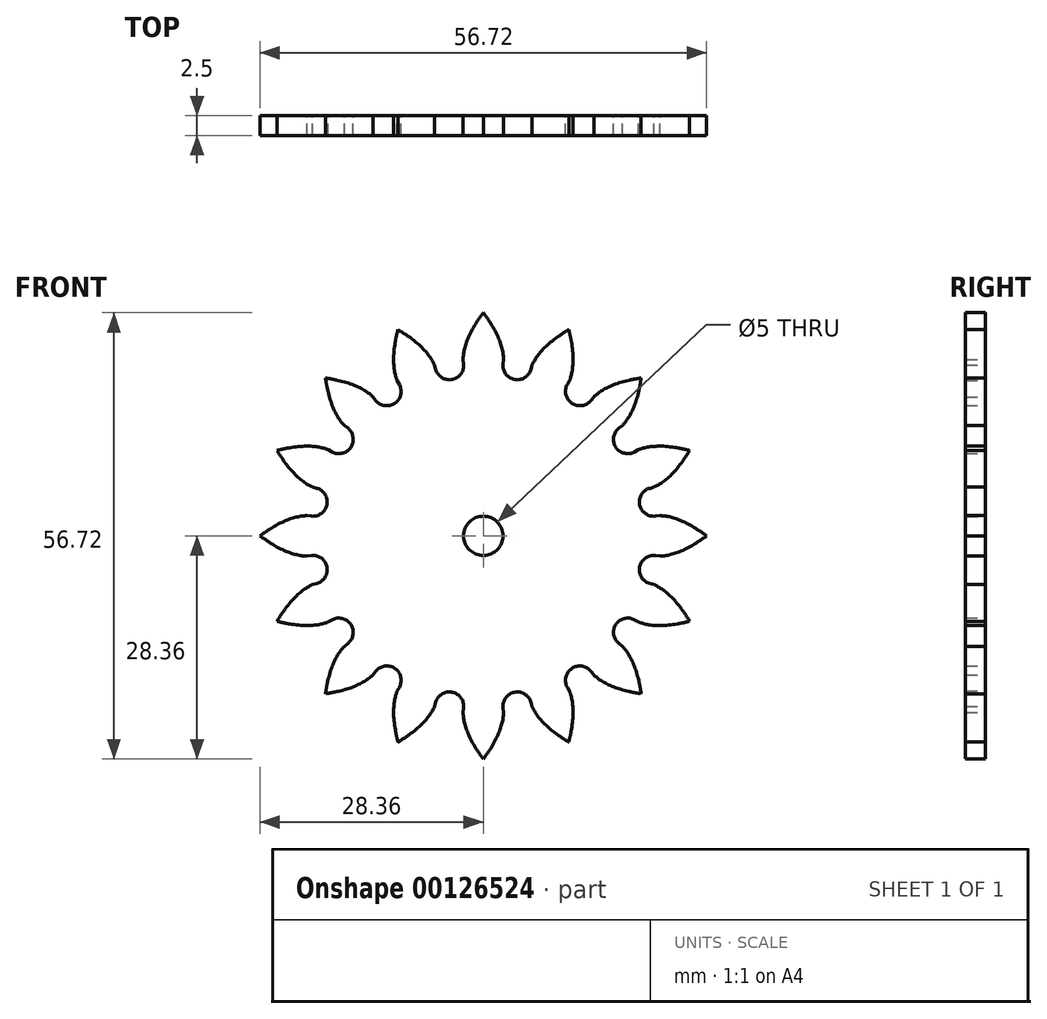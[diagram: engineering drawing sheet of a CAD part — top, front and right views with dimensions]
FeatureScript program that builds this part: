
annotation { "Feature Type Name" : "Feature", "Feature Type Description" : "" }
export const myFeature = defineFeature(function(context is Context, id is Id, definition is map)
    precondition{}
    {
        {
            assignVariable(context, id + "F0", {"name" : "NumberOfTeeth", "anyValue" : 16});
        }
        {
            var Q0;
            Q0=qCreatedBy(makeId("Front.planeOp"),FACE);
            var sketch = newSketch(context, id + "F1", { "sketchPlane" : qUnion([Q0])});
            skCircle(sketch, "E0", {"center": v(0, 0) * mm, "radius": 20.25 * mm});
            skSolve(sketch);
        }
        {
            var Q0;
            Q0=qSketchRegion(id+"F1",true);
            extrude(context, id + "F2", {"entities" : qUnion([Q0]), "depth" : 2.5 * mm});
        }
        {
            var Q0;
            Q0=qCreatedBy(makeId("Front.planeOp"),FACE);
            var sketch = newSketch(context, id + "F3", { "sketchPlane" : qUnion([Q0])});
            skCircle(sketch, "E1", {"center": v(0, 0) * mm, "radius": 24 * mm, "construction": true});
            skLineSegment(sketch, "E2", {"start": v(0, 0) * mm, "end": v(2.35, 23.88) * mm, "construction": true});
            skCircle(sketch, "E3.0", {"center": v(0, 0) * mm, "radius": 20.25 * mm, "construction": true});
            skLineSegment(sketch, "E4", {"start": v(0, 0) * mm, "end": v(4.68, 23.54) * mm, "construction": true});
            skCircle(sketch, "E5", {"center": v(0, 0) * mm, "radius": 22.55 * mm, "construction": true});
            skLineSegment(sketch, "E6", {"start": v(0, 0) * mm, "end": v(2.57, 22.4) * mm, "construction": true});
            skLineSegment(sketch, "E7", {"start": v(0, 0) * mm, "end": v(-3.43, 22.29) * mm, "construction": true});
            skLineSegment(sketch, "E8", {"start": v(0, 0) * mm, "end": v(-9.19, 20.6) * mm, "construction": true});
            skLineSegment(sketch, "E9", {"start": v(0, 0) * mm, "end": v(-14.3, 17.44) * mm, "construction": true});
            skLineSegment(sketch, "E10", {"start": v(0, 0) * mm, "end": v(-18.39, 13.06) * mm, "construction": true});
            skLineSegment(sketch, "E11", {"start": v(2.57, 22.4) * mm, "end": v(-3.43, 22.29) * mm, "construction": true});
            skLineSegment(sketch, "E12", {"start": v(-3.43, 22.29) * mm, "end": v(-9.19, 20.6) * mm, "construction": true});
            skLineSegment(sketch, "E13", {"start": v(-9.19, 20.6) * mm, "end": v(-14.3, 17.44) * mm, "construction": true});
            skLineSegment(sketch, "E14", {"start": v(-14.3, 17.44) * mm, "end": v(-18.39, 13.06) * mm, "construction": true});
            skLineSegment(sketch, "E15", {"start": v(0, 0) * mm, "end": v(-21.18, 7.75) * mm, "construction": true});
            skLineSegment(sketch, "E16", {"start": v(-18.39, 13.06) * mm, "end": v(-21.18, 7.75) * mm, "construction": true});
            skLineSegment(sketch, "E17", {"start": v(-3.43, 22.29) * mm, "end": v(2.5, 23.2) * mm, "construction": true});
            skLineSegment(sketch, "E18", {"start": v(-9.19, 20.6) * mm, "end": v(1.77, 25.49) * mm, "construction": true});
            skLineSegment(sketch, "E19", {"start": v(-14.3, 17.44) * mm, "end": v(-0.37, 28.85) * mm, "construction": true});
            skLineSegment(sketch, "E20", {"start": v(-18.39, 13.06) * mm, "end": v(-4.5, 32.63) * mm, "construction": true});
            skLineSegment(sketch, "E21", {"start": v(-21.18, 7.75) * mm, "end": v(-10.88, 35.92) * mm, "construction": true});
            skLineSegment(sketch, "E22", {"start": v(2.57, 22.4) * mm, "end": v(2.5, 21.85) * mm});
            skArc(sketch, "E23", {"start": v(2.5, 21.85) * mm, "mid": v(2.84, 20.57) * mm, "end": v(3.95, 19.86) * mm});
            skLineSegment(sketch, "E24", {"start": v(3.95, 19.86) * mm, "end": v(0, 0) * mm});
            skCircle(sketch, "E25", {"center": v(0, 0) * mm, "radius": 27 * mm, "construction": true});
            skFitSpline(sketch, "E26", {"points": [v(2.57, 22.4) * mm, v(2.5, 23.2) * mm, v(1.77, 25.49) * mm, v(-0.37, 28.85) * mm, v(-4.5, 32.63) * mm, v(-10.88, 35.92) * mm], "startDerivative": vector(0.21, 3.11) * mm, "endDerivative": vector(-9.59, 5.22) * mm});
            skFitSpline(sketch, "E27.MirrorCS", {"points": [v(-2.57, 22.4) * mm, v(-2.5, 23.2) * mm, v(-1.77, 25.49) * mm, v(0.37, 28.85) * mm, v(4.5, 32.63) * mm, v(10.88, 35.92) * mm], "startDerivative": vector(-0.21, 3.11) * mm, "endDerivative": vector(9.59, 5.22) * mm});
            skLineSegment(sketch, "E28.MirrorCS", {"start": v(-2.57, 22.4) * mm, "end": v(-2.5, 21.85) * mm});
            skArc(sketch, "E29.MirrorCS", {"start": v(-2.5, 21.85) * mm, "mid": v(-2.84, 20.57) * mm, "end": v(-3.95, 19.86) * mm});
            skLineSegment(sketch, "E30", {"start": v(-0.94, 26.98) * mm, "end": v(0.9, 27.05) * mm});
            skFitSpline(sketch, "E31.trimOffspring", {"points": [v(2.57, 22.4) * mm, v(2.5, 23.2) * mm, v(1.77, 25.49) * mm, v(-0.37, 28.85) * mm, v(-4.5, 32.63) * mm, v(-10.88, 35.92) * mm], "startDerivative": vector(0.21, 3.11) * mm, "endDerivative": vector(-9.59, 5.22) * mm});
            skLineSegment(sketch, "E32", {"start": v(-3.95, 19.86) * mm, "end": v(0, 0) * mm});
            skSolve(sketch);
        }
        {
            var Q0;
            Q0=qSketchRegion(id+"F3",true);
            extrude(context, id + "F4", {"entities" : qUnion([Q0]), "depth" : 2.5 * mm});
        }
        {
            var Q0;
            Q0=makeQuery(id+"F4.opExtrude","SWEPT_BODY",BODY,{"disambiguationData":[OSD([sQuery(id+"F3.wireOp",EDGE,"E22"),sQuery(id+"F3.wireOp",EDGE,"E23"),sQuery(id+"F3.wireOp",EDGE,"E24"),sQuery(id+"F3.wireOp",EDGE,"02dd0c5d-d1e8-4f79-863c-406f84435db1"),sQuery(id+"F3.wireOp",EDGE,"m1XDvlc8-NUZd-qkRk-q4Va-xkGgnuwNPfDB"),sQuery(id+"F3.wireOp",EDGE,"fcaf4da5-0803-456f-80d9-8ebba38615120.MirrorCS"),sQuery(id+"F3.wireOp",EDGE,"aedb47dc-a047-4e1f-8bb6-d5fbd5fdca930.MirrorCS"),sQuery(id+"F3.wireOp",EDGE,"a5371087-b1d2-494e-a018-3e77599f56c10.MirrorCS"),sQuery(id+"F3.wireOp",EDGE,"c3ac059d-0bc8-484a-9e2b-dc5b0a2fc6190.MirrorCS"),sQuery(id+"F3.wireOp",EDGE,"7677bc88-b94f-4734-94cb-964bed4e21a90.MirrorCS")])]});
            var Q1;
            Q1=sQuery(id+"F1.wireOp",EDGE,"E0");
            circularPattern(context, id + "F5", {"operationType" : NewBodyOperationType.ADD, "entities" : qUnion([Q0]), "axis" : qUnion([Q1]), "angle" : 360 * degree, "instanceCount" : getVariable(context, 'NumberOfTeeth'), "equalSpace" : true});
        }
        {
            var Q0;
            {var subQ0=makeQuery(id+"F4.opExtrude","CAP_FACE",FACE,{"disambiguationData":[OSD([sQuery(id+"F3.wireOp",EDGE,"1f885de5-3e7a-432a-b88a-3eaa30a7a401.0"),sQuery(id+"F3.wireOp",EDGE,"A7tLEwBN-HnOb-phWn-sB40-qaaEkIq7NDu9"),sQuery(id+"F3.wireOp",EDGE,"94f80f61-b426-4ec2-81a6-44f42ff73b0d"),sQuery(id+"F3.wireOp",EDGE,"3276b7df-17ce-42f5-8fef-bbce2681202d"),sQuery(id+"F3.wireOp",EDGE,"8cab6697-fc05-46dd-9d4d-494c43dbe1bc"),sQuery(id+"F3.wireOp",EDGE,"267e9553-86ea-40c7-a68d-067ff4e522c80.MirrorCS"),sQuery(id+"F3.wireOp",EDGE,"0081c8b5-e93b-4ec3-87cf-ae34b8c9de0e0.MirrorCS"),sQuery(id+"F3.wireOp",EDGE,"14eaaf62-2f47-4f70-a4e9-6a61db97f38f0.MirrorCS"),sQuery(id+"F3.wireOp",EDGE,"36c0f882-098c-494c-bc9e-4a3fa39534f60.MirrorCS")])],"isStart":false});Q0=makeQuery(id+"F5.boolean.opBoolean","MERGE",FACE,{"derivedFrom":[makeQuery(id+"F2.opExtrude","CAP_FACE",FACE,{"disambiguationData":[OSD([sQuery(id+"F1.wireOp",EDGE,"E0")])],"isStart":false}),subQ0,makeQuery(id+"F5.opPattern","COPY",FACE,{"derivedFrom":subQ0,"instanceName":"1"}),makeQuery(id+"F5.opPattern","COPY",FACE,{"derivedFrom":subQ0,"instanceName":"2"}),makeQuery(id+"F5.opPattern","COPY",FACE,{"derivedFrom":subQ0,"instanceName":"3"}),makeQuery(id+"F5.opPattern","COPY",FACE,{"derivedFrom":subQ0,"instanceName":"4"}),makeQuery(id+"F5.opPattern","COPY",FACE,{"derivedFrom":subQ0,"instanceName":"5"}),makeQuery(id+"F5.opPattern","COPY",FACE,{"derivedFrom":subQ0,"instanceName":"6"}),makeQuery(id+"F5.opPattern","COPY",FACE,{"derivedFrom":subQ0,"instanceName":"7"}),makeQuery(id+"F5.opPattern","COPY",FACE,{"derivedFrom":subQ0,"instanceName":"8"}),makeQuery(id+"F5.opPattern","COPY",FACE,{"derivedFrom":subQ0,"instanceName":"9"}),makeQuery(id+"F5.opPattern","COPY",FACE,{"derivedFrom":subQ0,"instanceName":"10"}),makeQuery(id+"F5.opPattern","COPY",FACE,{"derivedFrom":subQ0,"instanceName":"11"}),makeQuery(id+"F5.opPattern","COPY",FACE,{"derivedFrom":subQ0,"instanceName":"12"}),makeQuery(id+"F5.opPattern","COPY",FACE,{"derivedFrom":subQ0,"instanceName":"13"}),makeQuery(id+"F5.opPattern","COPY",FACE,{"derivedFrom":subQ0,"instanceName":"14"}),makeQuery(id+"F5.opPattern","COPY",FACE,{"derivedFrom":subQ0,"instanceName":"15"}),makeQuery(id+"F5.opPattern","COPY",FACE,{"derivedFrom":subQ0,"instanceName":"16"}),makeQuery(id+"F5.opPattern","COPY",FACE,{"derivedFrom":subQ0,"instanceName":"17"}),makeQuery(id+"F5.opPattern","COPY",FACE,{"derivedFrom":subQ0,"instanceName":"18"}),makeQuery(id+"F5.opPattern","COPY",FACE,{"derivedFrom":subQ0,"instanceName":"19"})]});}
            var sketch = newSketch(context, id + "F6", { "sketchPlane" : qUnion([Q0])});
            skCircle(sketch, "E33", {"center": v(0, 0) * mm, "radius": 2.5 * mm});
            skSolve(sketch);
        }
        {
            var Q0;
            Q0=qSketchRegion(id+"F6",true);
            extrude(context, id + "F7", {"entities" : qUnion([Q0]), "operationType" : NewBodyOperationType.REMOVE, "endBound" : BoundingType.THROUGH_ALL, "oppositeDirection" : true, "depth" : 25 * mm});
        }
    });
